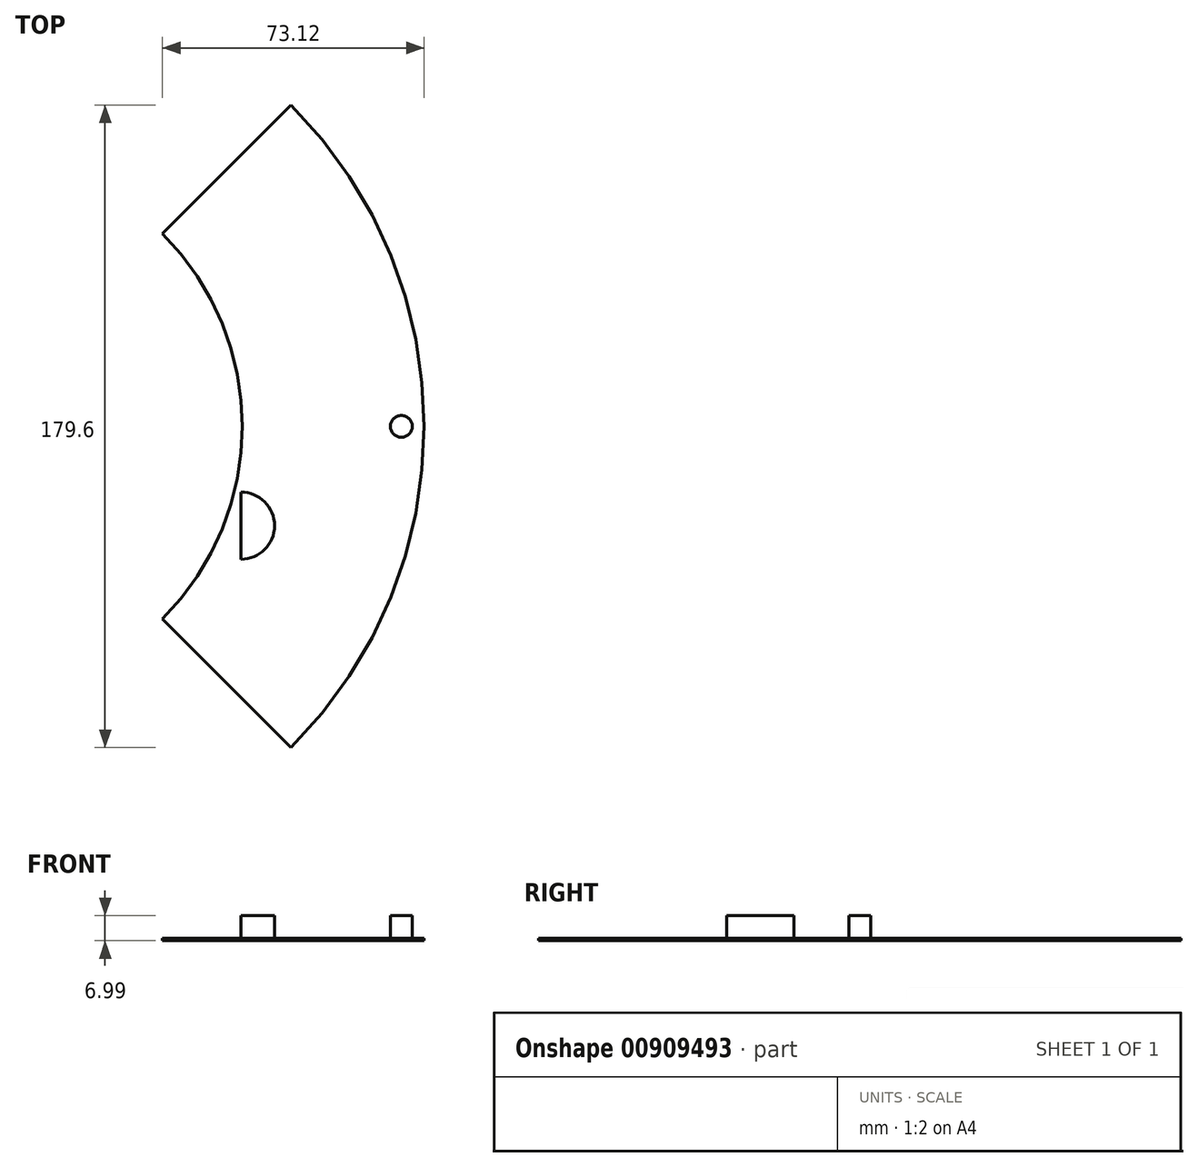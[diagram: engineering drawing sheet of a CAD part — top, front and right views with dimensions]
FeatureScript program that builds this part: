
annotation { "Feature Type Name" : "Feature", "Feature Type Description" : "" }
export const myFeature = defineFeature(function(context is Context, id is Id, definition is map)
    precondition{}
    {
        {
            var Q0;
            Q0=qCreatedBy(makeId("Top.planeOp"),FACE);
            var sketch = newSketch(context, id + "F0", { "sketchPlane" : qUnion([Q0])});
            skArc(sketch, "E0", {"start": v(89.8, -89.8) * mm, "mid": v(127, 0) * mm, "end": v(89.8, 89.8) * mm});
            skLineSegment(sketch, "E1", {"start": v(0, 0) * mm, "end": v(89.8, -89.8) * mm});
            skLineSegment(sketch, "E2", {"start": v(0, 0) * mm, "end": v(89.8, 89.8) * mm});
            skSolve(sketch);
        }
        {
            var Q0;
            Q0=makeQuery(id+"F0.imprint","IMPRINT",FACE,{"disambiguationData":[TD([[makeQuery(id+"F0.imprint","IMPRINT",EDGE,{"derivedFrom":sQuery(id+"F0.wireOp",EDGE,"E0")}),1.0]])]});
            extrude(context, id + "F1", {"entities" : qUnion([Q0]), "depth" : 0.64 * mm, "offsetDistance" : 25.4 * mm});
        }
        {
            var Q0;
            Q0=makeQuery(id+"F1.opExtrude","CAP_FACE",FACE,{"disambiguationData":[OSD([sQuery(id+"F0.wireOp",EDGE,"E0")])],"isStart":false});
            var sketch = newSketch(context, id + "F2", { "sketchPlane" : qUnion([Q0])});
            skCircle(sketch, "E3", {"center": v(120.65, 0) * mm, "radius": 3.05 * mm});
            skPoint(sketch, "E4.center", {"position": v(0, 0) * mm});
            skSolve(sketch);
        }
        {
            var Q0;
            Q0=makeQuery(id+"F1.opExtrude","CAP_FACE",FACE,{"disambiguationData":[OSD([sQuery(id+"F0.wireOp",EDGE,"E0")])],"isStart":false});
            var sketch = newSketch(context, id + "F3", { "sketchPlane" : qUnion([Q0])});
            skArc(sketch, "E5", {"start": v(53.88, -53.88) * mm, "mid": v(53.88, 53.88) * mm, "end": v(-53.88, 53.88) * mm});
            skLineSegment(sketch, "E6", {"start": v(-53.88, 53.88) * mm, "end": v(53.88, -53.88) * mm});
            skSolve(sketch);
        }
        {
            var Q0;
            {var subQ0=sQuery(id+"F3.wireOp",EDGE,"E5");Q0=makeQuery(id+"F3.imprint","IMPRINT",FACE,{"disambiguationData":[TD([[makeQuery(id+"F3.imprint","IMPRINT",EDGE,{"derivedFrom":subQ0}),-1.0]])]});}
            extrude(context, id + "F4", {"entities" : qUnion([Q0]), "operationType" : NewBodyOperationType.INTERSECT, "oppositeDirection" : true, "depth" : 25.4 * mm, "offsetDistance" : 25.4 * mm});
        }
        {
            var Q0;
            Q0=makeQuery(id+"F1.opExtrude","CAP_FACE",FACE,{"disambiguationData":[OSD([sQuery(id+"F0.wireOp",EDGE,"E0")])],"isStart":false});
            var sketch = newSketch(context, id + "F5", { "sketchPlane" : qUnion([Q0])});
            skArc(sketch, "E7", {"start": v(75.81, -37.17) * mm, "mid": v(85.2, -27.77) * mm, "end": v(75.81, -18.37) * mm});
            skLineSegment(sketch, "E8", {"start": v(75.81, -37.17) * mm, "end": v(75.81, -18.37) * mm});
            skSolve(sketch);
        }
        {
            var Q0;
            Q0 = qSketchRegion(id + "F2", true);
            extrude(context, id + "F6", {"entities" : qUnion([Q0]), "operationType" : NewBodyOperationType.ADD, "depth" : 6.35 * mm, "offsetDistance" : 25.4 * mm});
        }
        {
            var Q0;
            Q0 = qSketchRegion(id + "F5", true);
            extrude(context, id + "F7", {"entities" : qUnion([Q0]), "operationType" : NewBodyOperationType.ADD, "depth" : 6.35 * mm, "offsetDistance" : 25.4 * mm});
        }
    });
